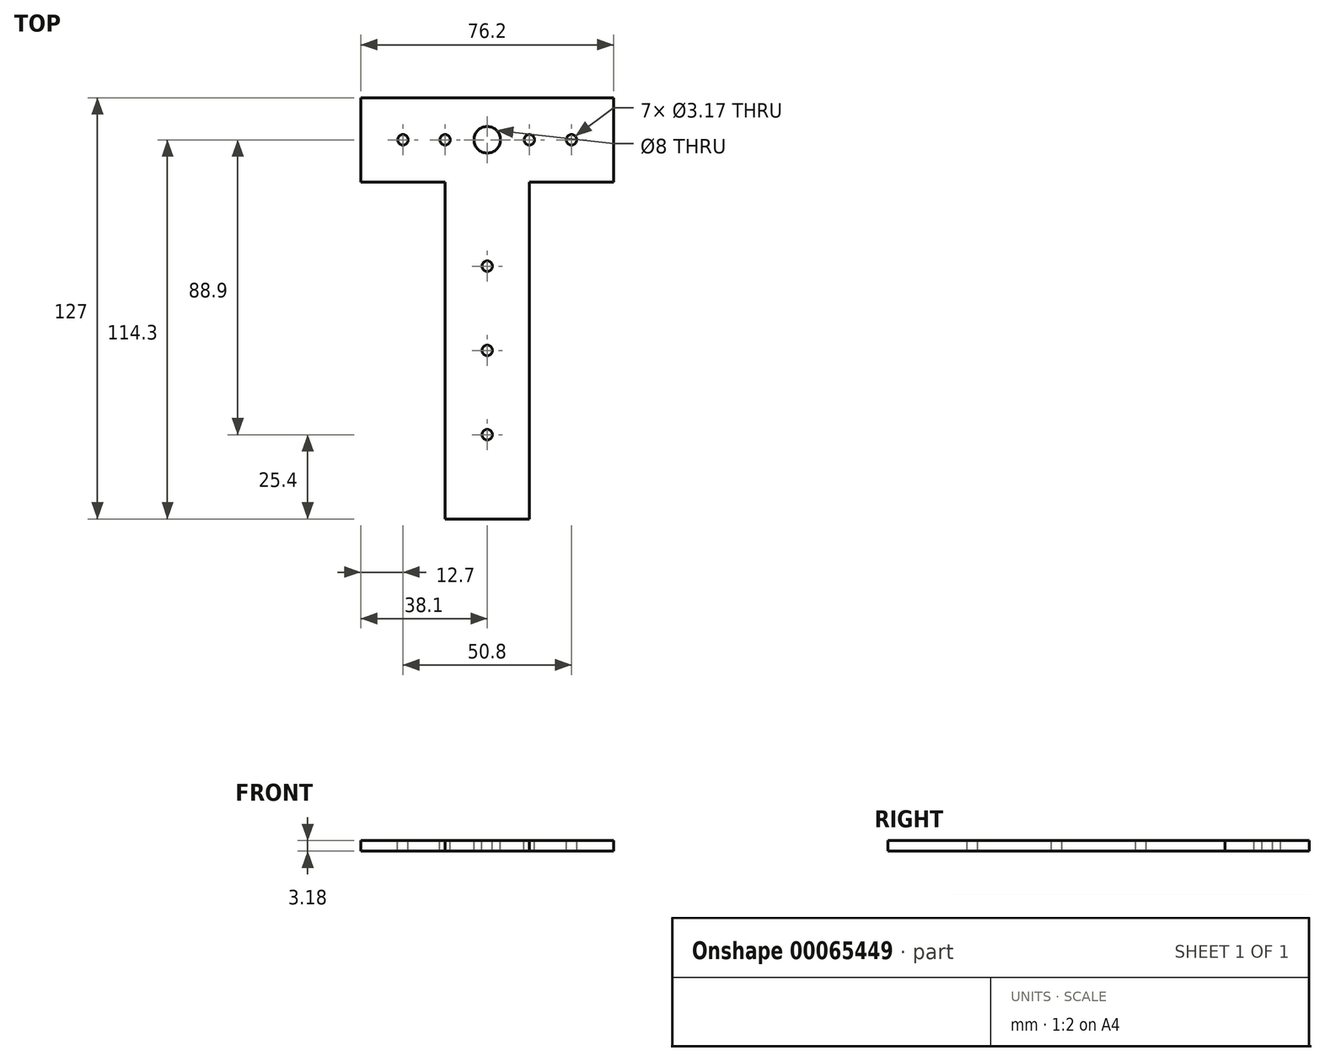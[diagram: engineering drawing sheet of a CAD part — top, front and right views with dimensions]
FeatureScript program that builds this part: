
annotation { "Feature Type Name" : "Feature", "Feature Type Description" : "" }
export const myFeature = defineFeature(function(context is Context, id is Id, definition is map)
    precondition{}
    {
        {
            var Q0;
            Q0=qCreatedBy(makeId("Top.planeOp"),FACE);
            var sketch = newSketch(context, id + "F0", { "sketchPlane" : qUnion([Q0])});
            skLineSegment(sketch, "E0.bottom", {"start": v(0, 0) * mm, "end": v(25.4, 0) * mm});
            skLineSegment(sketch, "E0.top", {"start": v(0, 25.4) * mm, "end": v(76.2, 25.4) * mm});
            skLineSegment(sketch, "E0.left", {"start": v(0, 0) * mm, "end": v(0, 25.4) * mm});
            skLineSegment(sketch, "E0.right", {"start": v(76.2, 0) * mm, "end": v(76.2, 25.4) * mm});
            skLineSegment(sketch, "E1.left", {"start": v(25.4, 0) * mm, "end": v(25.4, 0) * mm});
            skLineSegment(sketch, "E1.right", {"start": v(50.8, 0) * mm, "end": v(50.8, 0) * mm});
            skLineSegment(sketch, "E2.top", {"start": v(25.4, -101.6) * mm, "end": v(50.8, -101.6) * mm});
            skLineSegment(sketch, "E2.left", {"start": v(25.4, 0) * mm, "end": v(25.4, -101.6) * mm});
            skLineSegment(sketch, "E2.right", {"start": v(50.8, 0) * mm, "end": v(50.8, -101.6) * mm});
            skPoint(sketch, "E3.start.orphan", {"position": v(38.1, 0) * mm});
            skLineSegment(sketch, "E4.trimOffspring", {"start": v(50.8, 0) * mm, "end": v(76.2, 0) * mm});
            skSolve(sketch);
        }
        {
            var Q0;
            Q0=makeQuery(id+"F0.imprint","IMPRINT",FACE,{"disambiguationData":[TD([[makeQuery(id+"F0.imprint","IMPRINT",EDGE,{"derivedFrom":sQuery(id+"F0.wireOp",EDGE,"E0.bottom")}),1.0]])]});
            extrude(context, id + "F1", {"entities" : qUnion([Q0]), "depth" : 3.17 * mm});
        }
        {
            var Q0;
            Q0=makeQuery(id+"F1.opExtrude","CAP_FACE",FACE,{"disambiguationData":[OSD([sQuery(id+"F0.wireOp",EDGE,"E0.bottom"),sQuery(id+"F0.wireOp",EDGE,"E0.top"),sQuery(id+"F0.wireOp",EDGE,"E0.left"),sQuery(id+"F0.wireOp",EDGE,"E0.right"),sQuery(id+"F0.wireOp",EDGE,"E2.top"),sQuery(id+"F0.wireOp",EDGE,"E2.left"),sQuery(id+"F0.wireOp",EDGE,"E2.right"),sQuery(id+"F0.wireOp",EDGE,"E4.trimOffspring")])],"isStart":false});
            var sketch = newSketch(context, id + "F2", { "sketchPlane" : qUnion([Q0])});
            skLineSegment(sketch, "E5", {"start": v(0, 12.7) * mm, "end": v(76.2, 12.7) * mm});
            skLineSegment(sketch, "E6", {"start": v(76.2, 12.7) * mm, "end": v(63.5, 12.7) * mm});
            skLineSegment(sketch, "E7", {"start": v(63.5, 12.7) * mm, "end": v(50.8, 12.7) * mm});
            skLineSegment(sketch, "E8", {"start": v(50.8, 12.7) * mm, "end": v(38.1, 12.7) * mm});
            skLineSegment(sketch, "E9", {"start": v(38.1, 12.7) * mm, "end": v(25.4, 12.7) * mm});
            skLineSegment(sketch, "E10", {"start": v(25.4, 12.7) * mm, "end": v(12.7, 12.7) * mm});
            skLineSegment(sketch, "E11", {"start": v(12.7, 12.7) * mm, "end": v(0, 12.7) * mm});
            skLineSegment(sketch, "E12", {"start": v(38.1, 12.7) * mm, "end": v(38.1, 0) * mm});
            skLineSegment(sketch, "E13", {"start": v(38.1, 0) * mm, "end": v(38.1, -25.4) * mm});
            skLineSegment(sketch, "E14", {"start": v(38.1, -25.4) * mm, "end": v(38.1, -50.8) * mm});
            skLineSegment(sketch, "E15", {"start": v(38.1, -50.8) * mm, "end": v(38.1, -76.2) * mm});
            skLineSegment(sketch, "E16", {"start": v(38.1, -76.2) * mm, "end": v(38.1, -101.6) * mm});
            skLineSegment(sketch, "E17", {"start": v(38.1, -98.9) * mm, "end": v(38.1, -101.6) * mm});
            skSolve(sketch);
        }
        {
            var Q0;
            Q0=sQuery(id+"F2.wireOp",VERTEX,"E11.start");
            var Q1;
            Q1=sQuery(id+"F2.wireOp",VERTEX,"E10.start");
            var Q2;
            Q2=sQuery(id+"F2.wireOp",VERTEX,"E8.start");
            var Q3;
            Q3=sQuery(id+"F2.wireOp",VERTEX,"E7.start");
            var Q4;
            Q4=sQuery(id+"F2.wireOp",VERTEX,"E14.start");
            var Q5;
            Q5=sQuery(id+"F2.wireOp",VERTEX,"E15.start");
            var Q6;
            Q6=sQuery(id+"F2.wireOp",VERTEX,"E16.start");
            var Q7;
            Q7=makeQuery(id+"F1.opExtrude","SWEPT_BODY",BODY,{"disambiguationData":[OSD([sQuery(id+"F0.wireOp",EDGE,"E0.bottom"),sQuery(id+"F0.wireOp",EDGE,"E0.top"),sQuery(id+"F0.wireOp",EDGE,"E0.left"),sQuery(id+"F0.wireOp",EDGE,"E0.right"),sQuery(id+"F0.wireOp",EDGE,"E2.top"),sQuery(id+"F0.wireOp",EDGE,"E2.left"),sQuery(id+"F0.wireOp",EDGE,"E2.right"),sQuery(id+"F0.wireOp",EDGE,"E4.trimOffspring")])]});
            hole(context, id + "F3", {"style" : HoleStyle.SIMPLE, "holeDiameter" : 3.17 * mm, "endStyle" : HoleEndStyle.THROUGH, "locations" : qUnion([Q0, Q1, Q2, Q3, Q4, Q5, Q6]), "scope" : qUnion([Q7])});
        }
        {
            var Q0;
            Q0=makeQuery(id+"F1.opExtrude","CAP_FACE",FACE,{"disambiguationData":[OSD([sQuery(id+"F0.wireOp",EDGE,"E0.bottom"),sQuery(id+"F0.wireOp",EDGE,"E0.top"),sQuery(id+"F0.wireOp",EDGE,"E0.left"),sQuery(id+"F0.wireOp",EDGE,"E0.right"),sQuery(id+"F0.wireOp",EDGE,"E2.top"),sQuery(id+"F0.wireOp",EDGE,"E2.left"),sQuery(id+"F0.wireOp",EDGE,"E2.right"),sQuery(id+"F0.wireOp",EDGE,"E4.trimOffspring")])],"isStart":false});
            var sketch = newSketch(context, id + "F4", { "sketchPlane" : qUnion([Q0])});
            skLineSegment(sketch, "E18", {"start": v(0, 12.7) * mm, "end": v(76.2, 12.7) * mm});
            skCircle(sketch, "E19", {"center": v(38.1, 12.7) * mm, "radius": 4.32 * mm});
            skSolve(sketch);
        }
        {
            var Q0;
            Q0=sQuery(id+"F4.wireOp",VERTEX,"E19.center");
            var Q1;
            Q1=makeQuery(id+"F1.opExtrude","SWEPT_BODY",BODY,{"disambiguationData":[OSD([sQuery(id+"F0.wireOp",EDGE,"E0.bottom"),sQuery(id+"F0.wireOp",EDGE,"E0.top"),sQuery(id+"F0.wireOp",EDGE,"E0.left"),sQuery(id+"F0.wireOp",EDGE,"E0.right"),sQuery(id+"F0.wireOp",EDGE,"E2.top"),sQuery(id+"F0.wireOp",EDGE,"E2.left"),sQuery(id+"F0.wireOp",EDGE,"E2.right"),sQuery(id+"F0.wireOp",EDGE,"E4.trimOffspring")])]});
            hole(context, id + "F5", {"style" : HoleStyle.SIMPLE, "holeDiameter" : 8 * mm, "endStyle" : HoleEndStyle.THROUGH, "locations" : qUnion([Q0]), "scope" : qUnion([Q1])});
        }
    });
